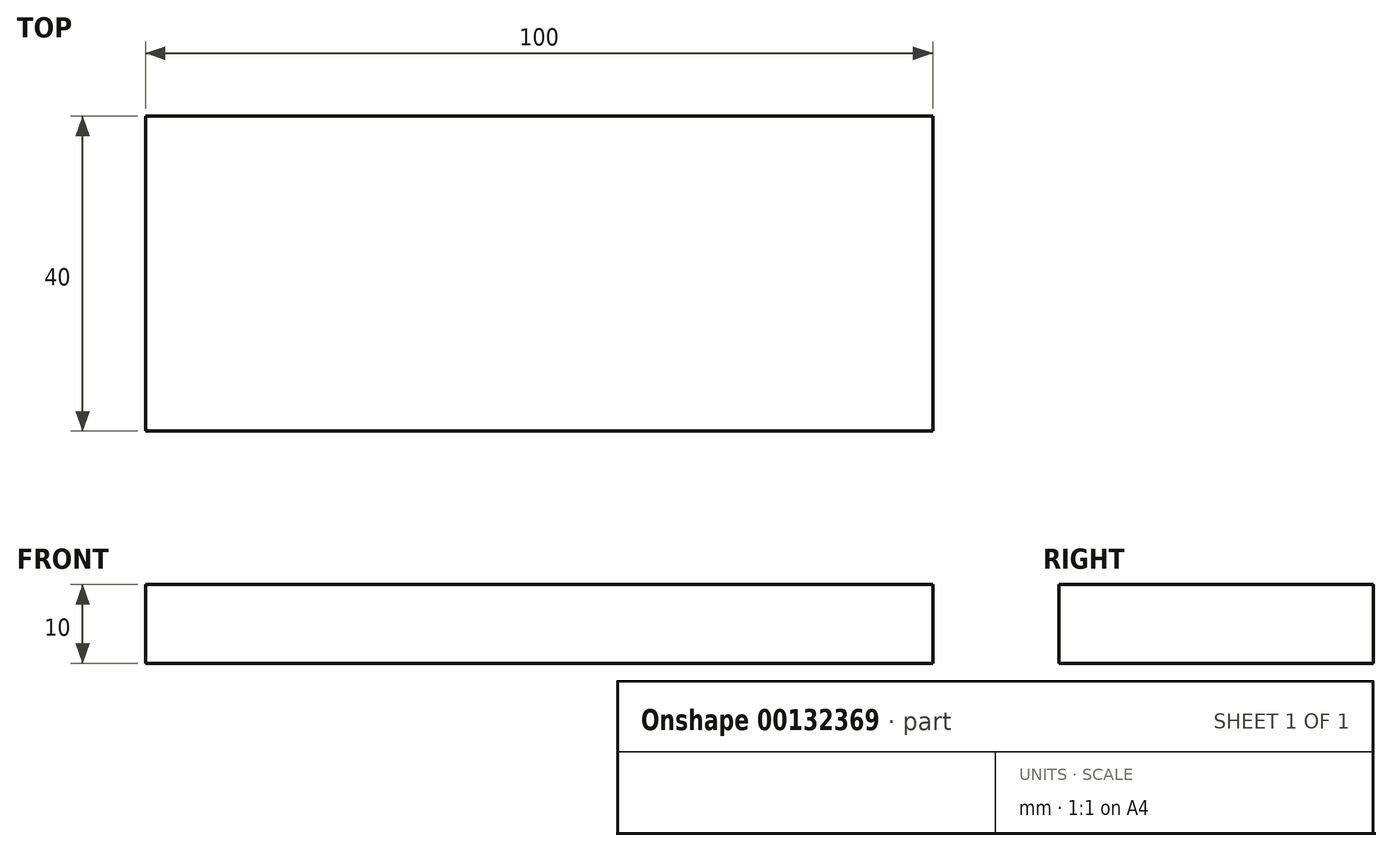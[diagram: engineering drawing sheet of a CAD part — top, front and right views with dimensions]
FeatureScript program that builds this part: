
annotation { "Feature Type Name" : "Feature", "Feature Type Description" : "" }
export const myFeature = defineFeature(function(context is Context, id is Id, definition is map)
    precondition{}
    {
        {
            var Q0;
            Q0=qCreatedBy(makeId("Top.planeOp"),FACE);
            var sketch = newSketch(context, id + "F0", { "sketchPlane" : qUnion([Q0])});
            skLineSegment(sketch, "E0.bottom", {"start": v(0, 0) * mm, "end": v(-100, 0) * mm});
            skLineSegment(sketch, "E0.top", {"start": v(0, 40) * mm, "end": v(-100, 40) * mm});
            skLineSegment(sketch, "E0.left", {"start": v(0, 0) * mm, "end": v(0, 40) * mm});
            skLineSegment(sketch, "E0.right", {"start": v(-100, 0) * mm, "end": v(-100, 40) * mm});
            skSolve(sketch);
        }
        {
            var Q0;
            Q0 = qSketchRegion(id + "F0", true);
            extrude(context, id + "F1", {"entities" : qUnion([Q0]), "depth" : 10 * mm});
        }
    });
